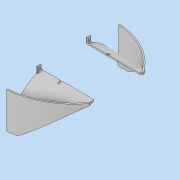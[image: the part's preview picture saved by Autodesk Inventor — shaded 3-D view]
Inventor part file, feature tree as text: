
AUTODESK INVENTOR PART (.ipt)
format: ipt  version: 2019 (Build 230136000, 136)  size: 858,112 bytes
history: native  units: mm
features: extrude x29, sketch x27, projected_geometry x12, other x4, mirror x3, loft x1, shell x1, fillet x1
ambient origin geometry x8: Origin, YZ Plane, XZ Plane, XY Plane, X Axis, Y Axis, Z Axis, Center Point
bodies: Body1 (feature_tree)
feature tree (78):
  sketch  "Эскиз4"
  other  "РабПлоскость1"
  sketch  "Эскиз5"
  loft  "Лофт1"
  extrude  "Выдавливание2"  Depth=100.0mm
  shell  "Оболочка1"  Thickness=17.0mm
  sketch  "Эскиз21"
  extrude  "Выдавливание15"  Depth=4.0mm
  extrude  "Выдавливание16"  Depth=35.0mm
  other  "РабПлоскость7"
  sketch  "Эскиз23"
  extrude  "Выдавливание17"  TaperAngle=0.0deg  [1 undecoded]
  extrude  "Выдавливание18"  TaperAngle=0.0deg  [1 undecoded]
  sketch  "Эскиз24"
  extrude  "Выдавливание19"  TaperAngle=0.0deg  [1 undecoded]
  extrude  "Выдавливание20"  Depth=130.0mm TaperAngle=0.0deg
  extrude  "Выдавливание21"  Depth=5.0mm
  mirror  "Зеркальное отражение2"
  other  "РабПлоскость12"
  extrude  "Выдавливание57"  Depth=2.0mm
  extrude  "Выдавливание62"  Depth=2.0mm
  mirror  "Зеркальное отражение5"
  extrude  "Выдавливание67"  Depth=2.0mm
  sketch  "Эскиз81"
  extrude  "Выдавливание68"  Depth=20.0mm
  extrude  "Выдавливание69"  Depth=10.0mm TaperAngle=0.0deg
  sketch  "Эскиз83"
  mirror  "Зеркальное отражение6"
  extrude  "Выдавливание70"  Depth=10.0mm TaperAngle=0.0deg
  sketch  "Эскиз84"
  extrude  "Выдавливание75"  Depth=143.802871mm
  extrude  "Выдавливание76"  TaperAngle=0.0deg  [1 undecoded]
  extrude  "Выдавливание77"  Depth=1.0mm TaperAngle=0.0deg
  extrude  "Выдавливание95"  Depth=5.0mm
  extrude  "Выдавливание96"  Depth=5.0mm
  extrude  "Выдавливание97"  Depth=2.0mm
  extrude  "Выдавливание98"  Depth=2.0mm
  extrude  "Выдавливание99"  Depth=5.0mm
  extrude  "Выдавливание100"  Depth=1.0mm TaperAngle=0.0deg
  extrude  "Выдавливание101"  Depth=3.0mm
  extrude  "Выдавливание102"  Depth=2.0mm
  extrude  "Выдавливание103"  Depth=6.0mm
  extrude  "Выдавливание104"  Depth=1.0mm TaperAngle=0.0deg
  fillet  "Сопряжение3"  Radius=2.0mm
  other  "РабПлоскость25"
  extrude  "Выдавливание105"  Depth=2.0mm
  extrude  "Выдавливание106"  Depth=2.0mm
  sketch  "Эскиз6"
  projected_geometry  "Спроецированная петля1"
  sketch  "Эскиз22"
  sketch  "Эскиз25"
  sketch  "Эскиз61"
  sketch  "Эскиз73"
  sketch  "Эскиз80"
  sketch  "Эскиз87"
  sketch  "Эскиз109"
  sketch  "Эскиз110"
  projected_geometry  "Спроецированная петля42"
  sketch  "Эскиз111"
  projected_geometry  "Спроецированная петля43"
  sketch  "Эскиз113"
  projected_geometry  "Спроецированная петля44"
  sketch  "Эскиз114"
  sketch  "Эскиз115"
  projected_geometry  "Спроецированная петля45"
  projected_geometry  "Спроецированная петля46"
  sketch  "Эскиз116"
  projected_geometry  "Спроецированная петля47"
  projected_geometry  "Спроецированная петля48"
  sketch  "Эскиз117"
  projected_geometry  "Спроецированная петля49"
  projected_geometry  "Спроецированная петля50"
  sketch  "Эскиз119"
  sketch  "Эскиз120"
  projected_geometry  "Спроецированная петля51"
  projected_geometry  "Спроецированная петля52"
  sketch  "Эскиз122"
  sketch  "Эскиз123"
note: 4 required parameter values undecoded (feature->parameter linkage not recoverable at this tier; creation-order binding heuristic only, values carry confidence <= 0.55)
